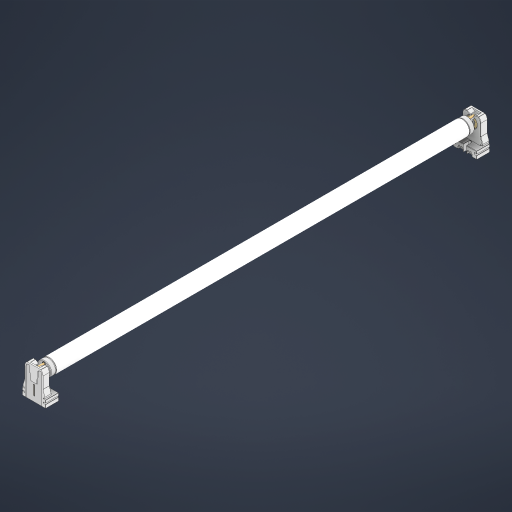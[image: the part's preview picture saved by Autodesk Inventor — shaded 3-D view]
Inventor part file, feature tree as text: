
AUTODESK INVENTOR PART (.ipt)
format: ipt  version: 2024 (Build 280153000, 153)  size: 1,358,848 bytes
history: native  units: mm
features: other x23, extrude x2, sketch x1
ambient origin geometry x8: Origin, YZ Plane, XZ Plane, XY Plane, X Axis, Y Axis, Z Axis, Center Point
bodies: Solid1 (feature_tree), Solid2 (feature_tree), Solid3 (feature_tree), Solid4 (feature_tree), Solid5 (feature_tree), Solid6 (feature_tree), Solid7 (feature_tree), Solid8 (feature_tree), Solid9 (feature_tree), Solid10 (feature_tree), Solid11 (feature_tree), Solid12 (feature_tree), Solid13 (feature_tree), Solid14 (feature_tree), Solid15 (feature_tree), Solid16 (feature_tree), Solid17 (feature_tree), Solid18 (feature_tree), Solid19 (feature_tree), Solid20 (feature_tree), Solid21 (feature_tree)
feature tree (26):
  other  "Lámpara Fluorescente T8.ipt"
  sketch  "Boceto1"  dims[d0=10000.0mm d1=1.0mm d2=5.0mm d3=1.0mm d4=0.0mm d5=1.0mm d6=5.0mm d7=1.0mm d8=0.0mm]
  extrude  "Extrusión1"  Depth=1.0mm
  extrude  "Extrusión2"  Depth=5.0mm
  other  "Solid1::Lámpara Fluorescente T8.ipt"
  other  "Solid2::Lámpara Fluorescente T8.ipt"
  other  "Solid3::Lámpara Fluorescente T8.ipt"
  other  "Solid4::Lámpara Fluorescente T8.ipt"
  other  "Solid5::Lámpara Fluorescente T8.ipt"
  other  "Solid6::Lámpara Fluorescente T8.ipt"
  other  "Solid7::Lámpara Fluorescente T8.ipt"
  other  "Solid8::Lámpara Fluorescente T8.ipt"
  other  "Solid9::Lámpara Fluorescente T8.ipt"
  other  "Solid10::Lámpara Fluorescente T8.ipt"
  other  "Solid11::Lámpara Fluorescente T8.ipt"
  other  "Solid12::Lámpara Fluorescente T8.ipt"
  other  "Solid13::Lámpara Fluorescente T8.ipt"
  other  "Solid14::Lámpara Fluorescente T8.ipt"
  other  "Solid15::Lámpara Fluorescente T8.ipt"
  other  "Solid16::Lámpara Fluorescente T8.ipt"
  other  "Solid17::Lámpara Fluorescente T8.ipt"
  other  "Solid18::Lámpara Fluorescente T8.ipt"
  other  "Solid19::Lámpara Fluorescente T8.ipt"
  other  "Solid20::Lámpara Fluorescente T8.ipt"
  other  "Solid21::Lámpara Fluorescente T8.ipt"
  other  "OperaciónIdentificador1"
